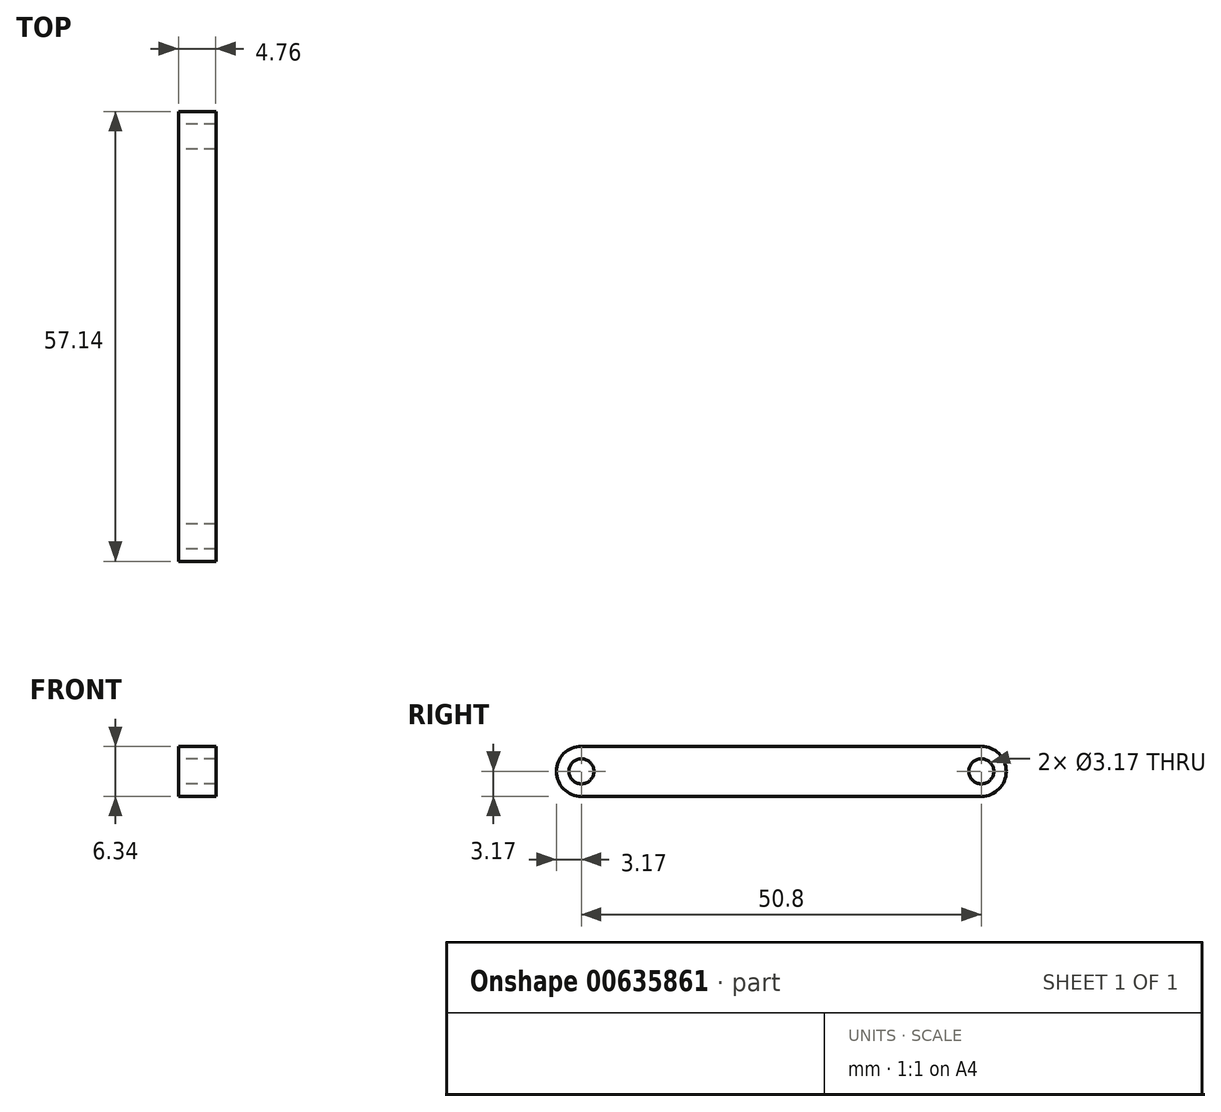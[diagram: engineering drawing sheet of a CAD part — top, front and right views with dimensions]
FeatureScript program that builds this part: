
annotation { "Feature Type Name" : "Feature", "Feature Type Description" : "" }
export const myFeature = defineFeature(function(context is Context, id is Id, definition is map)
    precondition{}
    {
        {
            var Q0;
            Q0=qCreatedBy(makeId("Right.planeOp"),FACE);
            var sketch = newSketch(context, id + "F0", { "sketchPlane" : qUnion([Q0])});
            skCircle(sketch, "E0", {"center": v(0, 0) * mm, "radius": 3.18 * mm});
            skCircle(sketch, "E1", {"center": v(50.8, 0) * mm, "radius": 3.18 * mm});
            skLineSegment(sketch, "E2", {"start": v(0, 3.18) * mm, "end": v(50.8, 3.18) * mm});
            skLineSegment(sketch, "E3", {"start": v(0, -3.18) * mm, "end": v(50.8, -3.18) * mm});
            skCircle(sketch, "E4", {"center": v(0, 0) * mm, "radius": 1.59 * mm});
            skCircle(sketch, "E5", {"center": v(50.8, 0) * mm, "radius": 1.59 * mm});
            skSolve(sketch);
        }
        {
            var Q0;
            {var subQ0=sQuery(id+"F0.wireOp",EDGE,"E2");Q0=makeQuery(id+"F0.imprint","IMPRINT",FACE,{"disambiguationData":[TD([[makeQuery(id+"F0.imprint","IMPRINT",EDGE,{"derivedFrom":subQ0}),-1.0]])]});}
            var Q1;
            Q1=makeQuery(id+"F0.imprint","IMPRINT",FACE,{"disambiguationData":[TD([[makeQuery(id+"F0.imprint","IMPRINT",EDGE,{"derivedFrom":sQuery(id+"F0.wireOp",EDGE,"E4")}),-1.0]])]});
            var Q2;
            Q2=makeQuery(id+"F0.imprint","IMPRINT",FACE,{"disambiguationData":[TD([[makeQuery(id+"F0.imprint","IMPRINT",EDGE,{"derivedFrom":sQuery(id+"F0.wireOp",EDGE,"E5")}),-1.0]])]});
            extrude(context, id + "F1", {"entities" : qUnion([Q0, Q1, Q2]), "depth" : 4.76 * mm, "offsetDistance" : 25.4 * mm});
        }
    });
